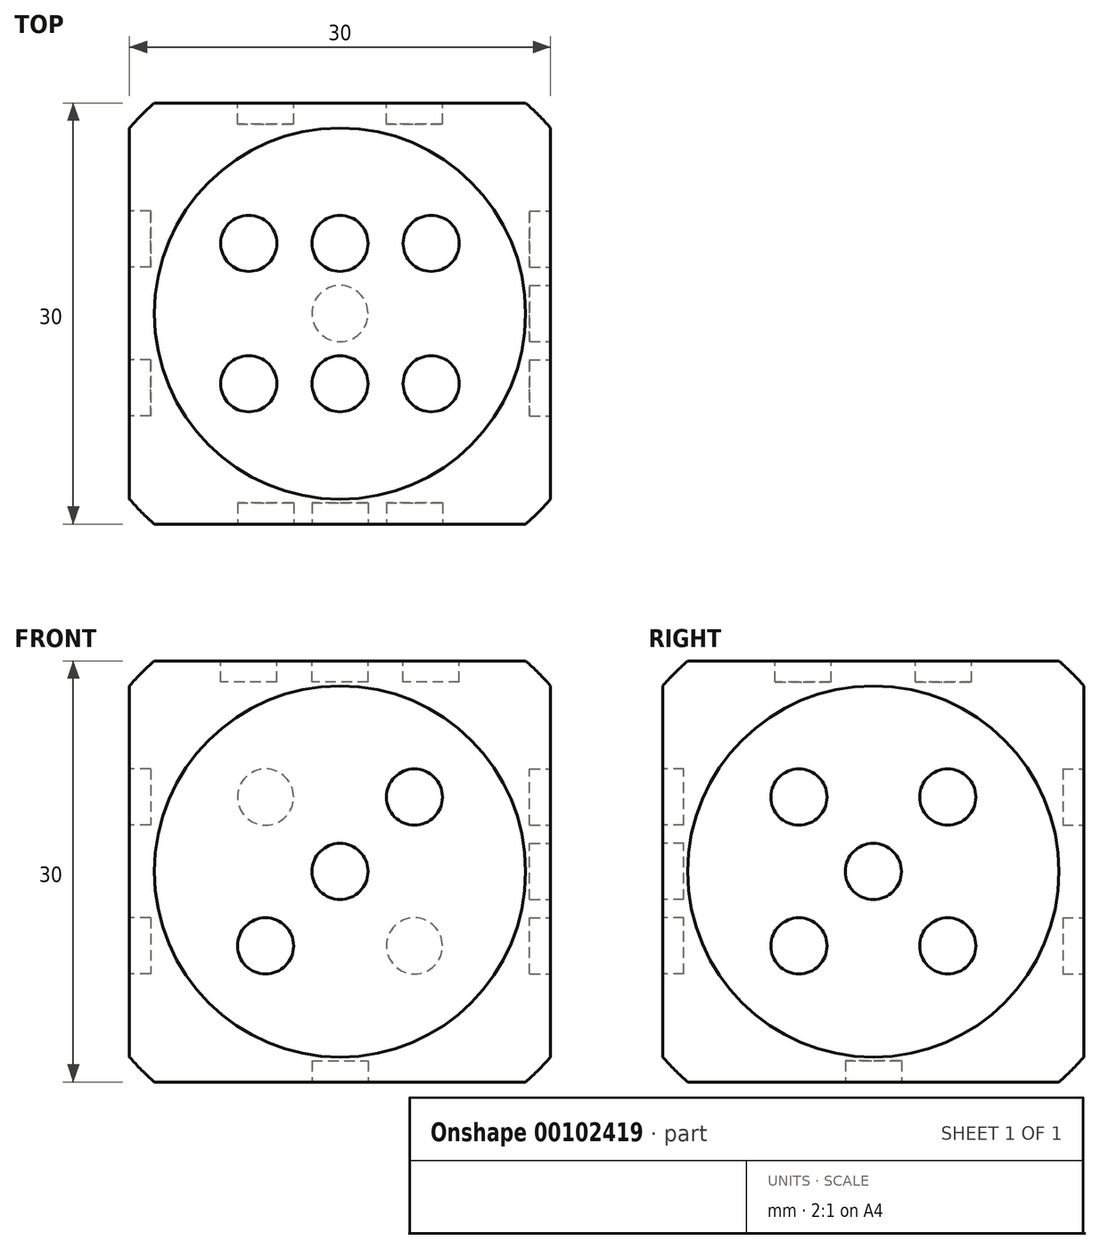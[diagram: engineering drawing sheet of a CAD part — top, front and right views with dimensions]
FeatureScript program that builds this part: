
annotation { "Feature Type Name" : "Feature", "Feature Type Description" : "" }
export const myFeature = defineFeature(function(context is Context, id is Id, definition is map)
    precondition{}
    {
        {
            var Q0;
            Q0=qCreatedBy(makeId("Top.planeOp"),FACE);
            var sketch = newSketch(context, id + "F0", { "sketchPlane" : qUnion([Q0])});
            skLineSegment(sketch, "E0.bottom", {"start": v(-15, 15) * mm, "end": v(15, 15) * mm});
            skLineSegment(sketch, "E0.top", {"start": v(-15, -15) * mm, "end": v(15, -15) * mm});
            skLineSegment(sketch, "E0.left", {"start": v(-15, 15) * mm, "end": v(-15, -15) * mm});
            skLineSegment(sketch, "E0.right", {"start": v(15, 15) * mm, "end": v(15, -15) * mm});
            skLineSegment(sketch, "E1", {"start": v(-15, -15) * mm, "end": v(15, 15) * mm, "construction": true});
            skSolve(sketch);
        }
        {
            var Q0;
            Q0 = qSketchRegion(id + "F0", true);
            extrude(context, id + "F1", {"entities" : qUnion([Q0]), "endBound" : BoundingType.SYMMETRIC, "depth" : 30 * mm});
        }
        {
            var Q0;
            Q0=qCreatedBy(makeId("Top.planeOp"),FACE);
            var sketch = newSketch(context, id + "F2", { "sketchPlane" : qUnion([Q0])});
            skArc(sketch, "E2", {"start": v(0, 20) * mm, "mid": v(20, 0) * mm, "end": v(0, -20) * mm});
            skLineSegment(sketch, "E3", {"start": v(0, 20) * mm, "end": v(0, -20) * mm});
            skSolve(sketch);
        }
        {
            var Q0;
            Q0 = qSketchRegion(id + "F2", true);
            var Q1;
            Q1=sQuery(id+"F2.wireOp",EDGE,"E3");
            revolve(context, id + "F3", {"entities" : qUnion([Q0]), "axis" : qUnion([Q1]), "revolveType" : RevolveType.FULL});
        }
        {
            var Q0;
            Q0=makeQuery(id+"F1.opExtrude","SWEPT_BODY",BODY,{"disambiguationData":[OSD([sQuery(id+"F0.wireOp",EDGE,"E0.bottom"),sQuery(id+"F0.wireOp",EDGE,"E0.top"),sQuery(id+"F0.wireOp",EDGE,"E0.left"),sQuery(id+"F0.wireOp",EDGE,"E0.right")])]});
            var Q1;
            Q1=makeQuery(id+"F3.opRevolve","SWEPT_BODY",BODY,{"disambiguationData":[OSD([sQuery(id+"F2.wireOp",EDGE,"E2"),sQuery(id+"F2.wireOp",EDGE,"E3")])]});
            booleanBodies(context, id + "F4", {"operationType" : BooleanOperationType.INTERSECTION, "tools" : qUnion([Q0, Q1])});
        }
        {
            var Q0;
            Q0=makeQuery(id+"F1.opExtrude","CAP_FACE",FACE,{"disambiguationData":[OSD([sQuery(id+"F0.wireOp",EDGE,"E0.bottom"),sQuery(id+"F0.wireOp",EDGE,"E0.top"),sQuery(id+"F0.wireOp",EDGE,"E0.left"),sQuery(id+"F0.wireOp",EDGE,"E0.right")])],"isStart":true});
            var sketch = newSketch(context, id + "F5", { "sketchPlane" : qUnion([Q0])});
            skCircle(sketch, "E4", {"center": v(0, 0) * mm, "radius": 2 * mm});
            skSolve(sketch);
        }
        {
            var Q0;
            Q0 = qSketchRegion(id + "F5", true);
            extrude(context, id + "F6", {"entities" : qUnion([Q0]), "operationType" : NewBodyOperationType.REMOVE, "oppositeDirection" : true, "depth" : 1.5 * mm});
        }
        {
            var Q0;
            Q0=makeQuery(id+"F1.opExtrude","CAP_FACE",FACE,{"disambiguationData":[OSD([sQuery(id+"F0.wireOp",EDGE,"E0.bottom"),sQuery(id+"F0.wireOp",EDGE,"E0.top"),sQuery(id+"F0.wireOp",EDGE,"E0.left"),sQuery(id+"F0.wireOp",EDGE,"E0.right")])],"isStart":false});
            var sketch = newSketch(context, id + "F7", { "sketchPlane" : qUnion([Q0])});
            skLineSegment(sketch, "E5.bottom", {"start": v(6.5, 5) * mm, "end": v(-6.5, 5) * mm, "construction": true});
            skLineSegment(sketch, "E5.top", {"start": v(6.5, -5) * mm, "end": v(-6.5, -5) * mm, "construction": true});
            skLineSegment(sketch, "E5.left", {"start": v(6.5, 5) * mm, "end": v(6.5, -5) * mm, "construction": true});
            skLineSegment(sketch, "E5.right", {"start": v(-6.5, 5) * mm, "end": v(-6.5, -5) * mm, "construction": true});
            skLineSegment(sketch, "E6", {"start": v(-6.5, 5) * mm, "end": v(6.5, -5) * mm, "construction": true});
            skCircle(sketch, "E7", {"center": v(0, 5) * mm, "radius": 2 * mm});
            skCircle(sketch, "E8", {"center": v(6.5, 5) * mm, "radius": 2 * mm});
            skLineSegment(sketch, "E9", {"start": v(0, 5) * mm, "end": v(0, 0) * mm, "construction": true});
            skLineSegment(sketch, "E10", {"start": v(0, 0) * mm, "end": v(6.5, 0) * mm, "construction": true});
            skCircle(sketch, "E11.MirrorC", {"center": v(0, -5) * mm, "radius": 2 * mm});
            skCircle(sketch, "E12.MirrorC", {"center": v(6.5, -5) * mm, "radius": 2 * mm});
            skCircle(sketch, "E13.MirrorC", {"center": v(-6.5, -5) * mm, "radius": 2 * mm});
            skCircle(sketch, "E14.MirrorC", {"center": v(-6.5, 5) * mm, "radius": 2 * mm});
            skSolve(sketch);
        }
        {
            var Q0;
            Q0 = qSketchRegion(id + "F7", true);
            extrude(context, id + "F8", {"entities" : qUnion([Q0]), "operationType" : NewBodyOperationType.REMOVE, "oppositeDirection" : true, "depth" : 1.5 * mm});
        }
        {
            var Q0;
            Q0=makeQuery(id+"F1.opExtrude","SWEPT_FACE",FACE,{"disambiguationData":[OSD([sQuery(id+"F0.wireOp",EDGE,"E0.left")])]});
            var sketch = newSketch(context, id + "F9", { "sketchPlane" : qUnion([Q0])});
            skLineSegment(sketch, "E15", {"start": v(0, 10.6) * mm, "end": v(0, 0) * mm, "construction": true});
            skLineSegment(sketch, "E16", {"start": v(0, 0) * mm, "end": v(10.6, 0) * mm, "construction": true});
            skLineSegment(sketch, "E17", {"start": v(10.6, 0) * mm, "end": v(0, 10.6) * mm, "construction": true});
            skCircle(sketch, "E18", {"center": v(5.3, 5.3) * mm, "radius": 2 * mm});
            skLineSegment(sketch, "E19", {"start": v(0, 0) * mm, "end": v(-4.45, 4.45) * mm, "construction": true});
            skCircle(sketch, "E20.MirrorC", {"center": v(-5.3, -5.3) * mm, "radius": 2 * mm});
            skSolve(sketch);
        }
        {
            var Q0;
            Q0 = qSketchRegion(id + "F9", true);
            extrude(context, id + "F10", {"entities" : qUnion([Q0]), "operationType" : NewBodyOperationType.REMOVE, "oppositeDirection" : true, "depth" : 1.5 * mm});
        }
        {
            var Q0;
            Q0=makeQuery(id+"F1.opExtrude","SWEPT_FACE",FACE,{"disambiguationData":[OSD([sQuery(id+"F0.wireOp",EDGE,"E0.right")])]});
            var sketch = newSketch(context, id + "F11", { "sketchPlane" : qUnion([Q0])});
            skLineSegment(sketch, "E21.bottom", {"start": v(-5.3, 5.3) * mm, "end": v(5.3, 5.3) * mm, "construction": true});
            skLineSegment(sketch, "E21.top", {"start": v(-5.3, -5.3) * mm, "end": v(5.3, -5.3) * mm, "construction": true});
            skLineSegment(sketch, "E21.left", {"start": v(-5.3, 5.3) * mm, "end": v(-5.3, -5.3) * mm, "construction": true});
            skLineSegment(sketch, "E21.right", {"start": v(5.3, 5.3) * mm, "end": v(5.3, -5.3) * mm, "construction": true});
            skLineSegment(sketch, "E22", {"start": v(-5.3, -5.3) * mm, "end": v(5.3, 5.3) * mm, "construction": true});
            skCircle(sketch, "E23", {"center": v(5.3, 5.3) * mm, "radius": 2 * mm});
            skCircle(sketch, "E24", {"center": v(0, 0) * mm, "radius": 2 * mm});
            skLineSegment(sketch, "E25", {"start": v(0, 5.3) * mm, "end": v(0, 0) * mm, "construction": true});
            skLineSegment(sketch, "E26", {"start": v(5.3, 0) * mm, "end": v(0, 0) * mm, "construction": true});
            skCircle(sketch, "E27.MirrorC", {"center": v(-5.3, 5.3) * mm, "radius": 2 * mm});
            skCircle(sketch, "E28.MirrorC", {"center": v(5.3, -5.3) * mm, "radius": 2 * mm});
            skCircle(sketch, "E29.MirrorC", {"center": v(-5.3, -5.3) * mm, "radius": 2 * mm});
            skSolve(sketch);
        }
        {
            var Q0;
            Q0 = qSketchRegion(id + "F11", true);
            extrude(context, id + "F12", {"entities" : qUnion([Q0]), "operationType" : NewBodyOperationType.REMOVE, "oppositeDirection" : true, "depth" : 1.5 * mm});
        }
        {
            var Q0;
            Q0=makeQuery(id+"F1.opExtrude","SWEPT_FACE",FACE,{"disambiguationData":[OSD([sQuery(id+"F0.wireOp",EDGE,"E0.top")])]});
            var sketch = newSketch(context, id + "F13", { "sketchPlane" : qUnion([Q0])});
            skLineSegment(sketch, "E30.bottom", {"start": v(-5.3, 5.3) * mm, "end": v(5.3, 5.3) * mm, "construction": true});
            skLineSegment(sketch, "E30.top", {"start": v(-5.3, -5.3) * mm, "end": v(5.3, -5.3) * mm, "construction": true});
            skLineSegment(sketch, "E30.left", {"start": v(-5.3, 5.3) * mm, "end": v(-5.3, -5.3) * mm, "construction": true});
            skLineSegment(sketch, "E30.right", {"start": v(5.3, 5.3) * mm, "end": v(5.3, -5.3) * mm, "construction": true});
            skLineSegment(sketch, "E31", {"start": v(-5.3, -5.3) * mm, "end": v(5.3, 5.3) * mm, "construction": true});
            skCircle(sketch, "E32", {"center": v(5.3, 5.3) * mm, "radius": 2 * mm});
            skCircle(sketch, "E33", {"center": v(0, 0) * mm, "radius": 2 * mm});
            skCircle(sketch, "E34", {"center": v(-5.3, -5.3) * mm, "radius": 2 * mm});
            skSolve(sketch);
        }
        {
            var Q0;
            Q0 = qSketchRegion(id + "F13", true);
            extrude(context, id + "F14", {"entities" : qUnion([Q0]), "operationType" : NewBodyOperationType.REMOVE, "oppositeDirection" : true, "depth" : 1.5 * mm});
        }
        {
            var Q0;
            Q0=makeQuery(id+"F1.opExtrude","SWEPT_FACE",FACE,{"disambiguationData":[OSD([sQuery(id+"F0.wireOp",EDGE,"E0.bottom")])]});
            var sketch = newSketch(context, id + "F15", { "sketchPlane" : qUnion([Q0])});
            skLineSegment(sketch, "E35.bottom", {"start": v(-5.3, 5.3) * mm, "end": v(5.3, 5.3) * mm, "construction": true});
            skLineSegment(sketch, "E35.top", {"start": v(-5.3, -5.3) * mm, "end": v(5.3, -5.3) * mm, "construction": true});
            skLineSegment(sketch, "E35.left", {"start": v(-5.3, 5.3) * mm, "end": v(-5.3, -5.3) * mm, "construction": true});
            skLineSegment(sketch, "E35.right", {"start": v(5.3, 5.3) * mm, "end": v(5.3, -5.3) * mm, "construction": true});
            skLineSegment(sketch, "E36", {"start": v(-5.3, -5.3) * mm, "end": v(5.3, 5.3) * mm, "construction": true});
            skCircle(sketch, "E37", {"center": v(5.3, 5.3) * mm, "radius": 2 * mm});
            skLineSegment(sketch, "E38", {"start": v(0, 5.3) * mm, "end": v(0, -5.3) * mm, "construction": true});
            skLineSegment(sketch, "E39", {"start": v(-5.3, 0) * mm, "end": v(5.3, 0) * mm, "construction": true});
            skCircle(sketch, "E40.MirrorC", {"center": v(-5.3, 5.3) * mm, "radius": 2 * mm});
            skCircle(sketch, "E41.MirrorC", {"center": v(5.3, -5.3) * mm, "radius": 2 * mm});
            skCircle(sketch, "E42.MirrorC", {"center": v(-5.3, -5.3) * mm, "radius": 2 * mm});
            skSolve(sketch);
        }
        {
            var Q0;
            Q0 = qSketchRegion(id + "F15", true);
            extrude(context, id + "F16", {"entities" : qUnion([Q0]), "operationType" : NewBodyOperationType.REMOVE, "oppositeDirection" : true, "depth" : 1.5 * mm});
        }
    });
